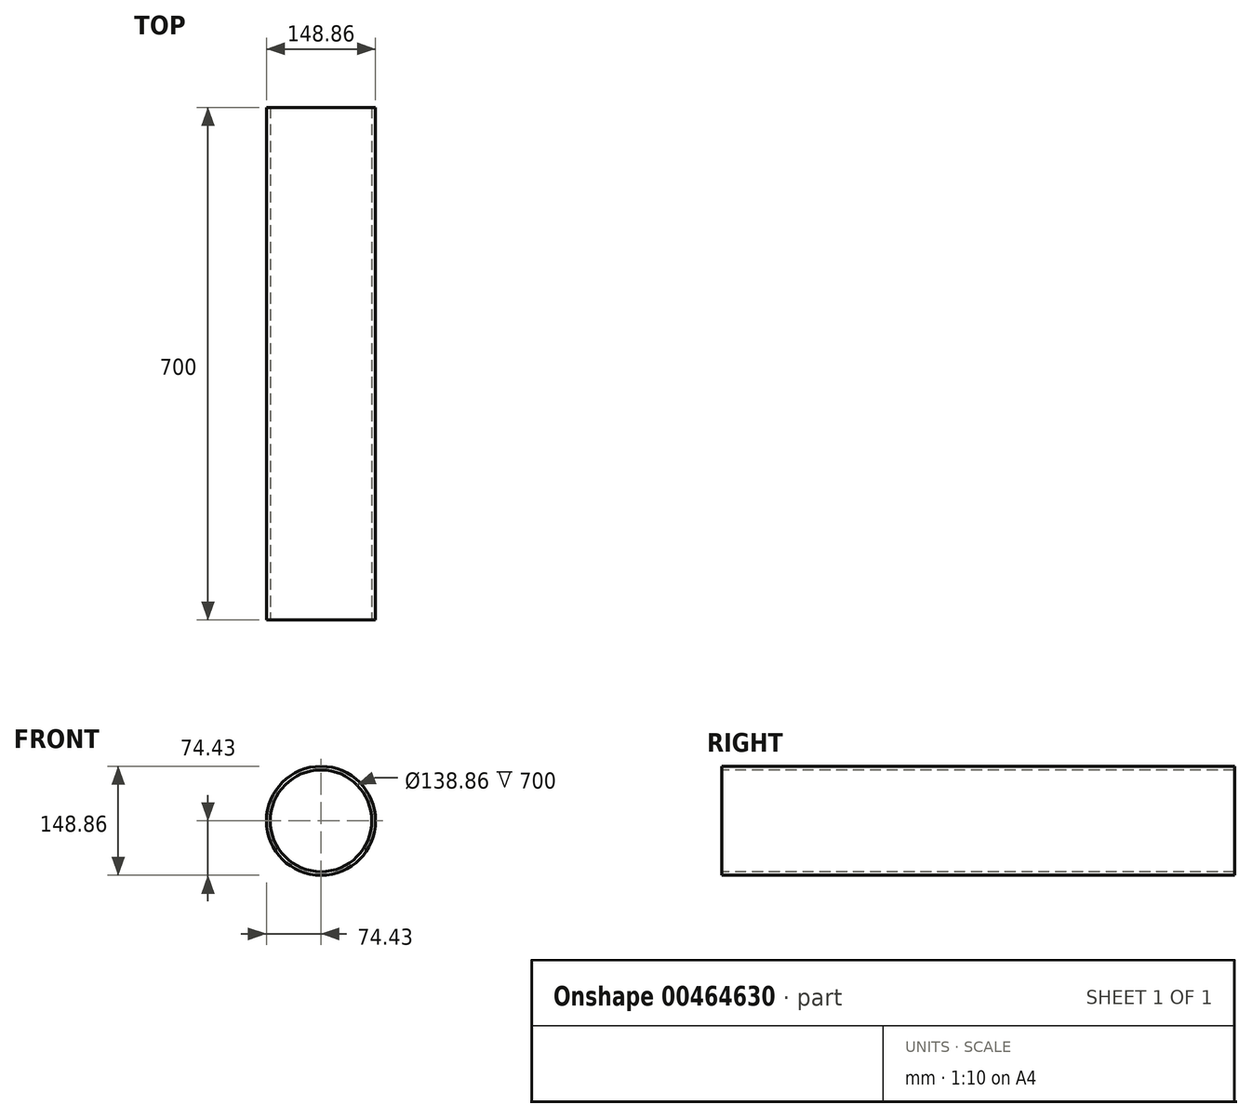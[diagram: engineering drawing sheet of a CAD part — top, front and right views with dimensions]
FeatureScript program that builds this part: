
annotation { "Feature Type Name" : "Feature", "Feature Type Description" : "" }
export const myFeature = defineFeature(function(context is Context, id is Id, definition is map)
    precondition{}
    {
        {
            var Q0;
            Q0=qCreatedBy(makeId("Front.planeOp"),FACE);
            var sketch = newSketch(context, id + "F0", { "sketchPlane" : qUnion([Q0])});
            skCircle(sketch, "E0", {"center": v(0, 0) * mm, "radius": 74.43 * mm});
            skCircle(sketch, "E1.0", {"center": v(0, 0) * mm, "radius": 69.43 * mm});
            skSolve(sketch);
        }
        {
            var Q0;
            Q0 = qSketchRegion(id + "F0", true);
            extrude(context, id + "F1", {"entities" : qUnion([Q0]), "oppositeDirection" : true, "depth" : 700 * mm, "offsetDistance" : 25 * mm});
        }
        {
            var Q0;
            Q0=makeQuery(id+"F1.opExtrude","SWEPT_BODY",BODY,{"disambiguationData":[OSD([sQuery(id+"F0.wireOp",EDGE,"E0")])]});
            transform(context, id + "F2", {"entities" : qUnion([Q0]), "transformType" : TransformType.TRANSLATION_3D, "dx" : 0 * mm, "dy" : -413 * mm, "dz" : 0 * mm, "makeCopy" : false});
        }
    });
